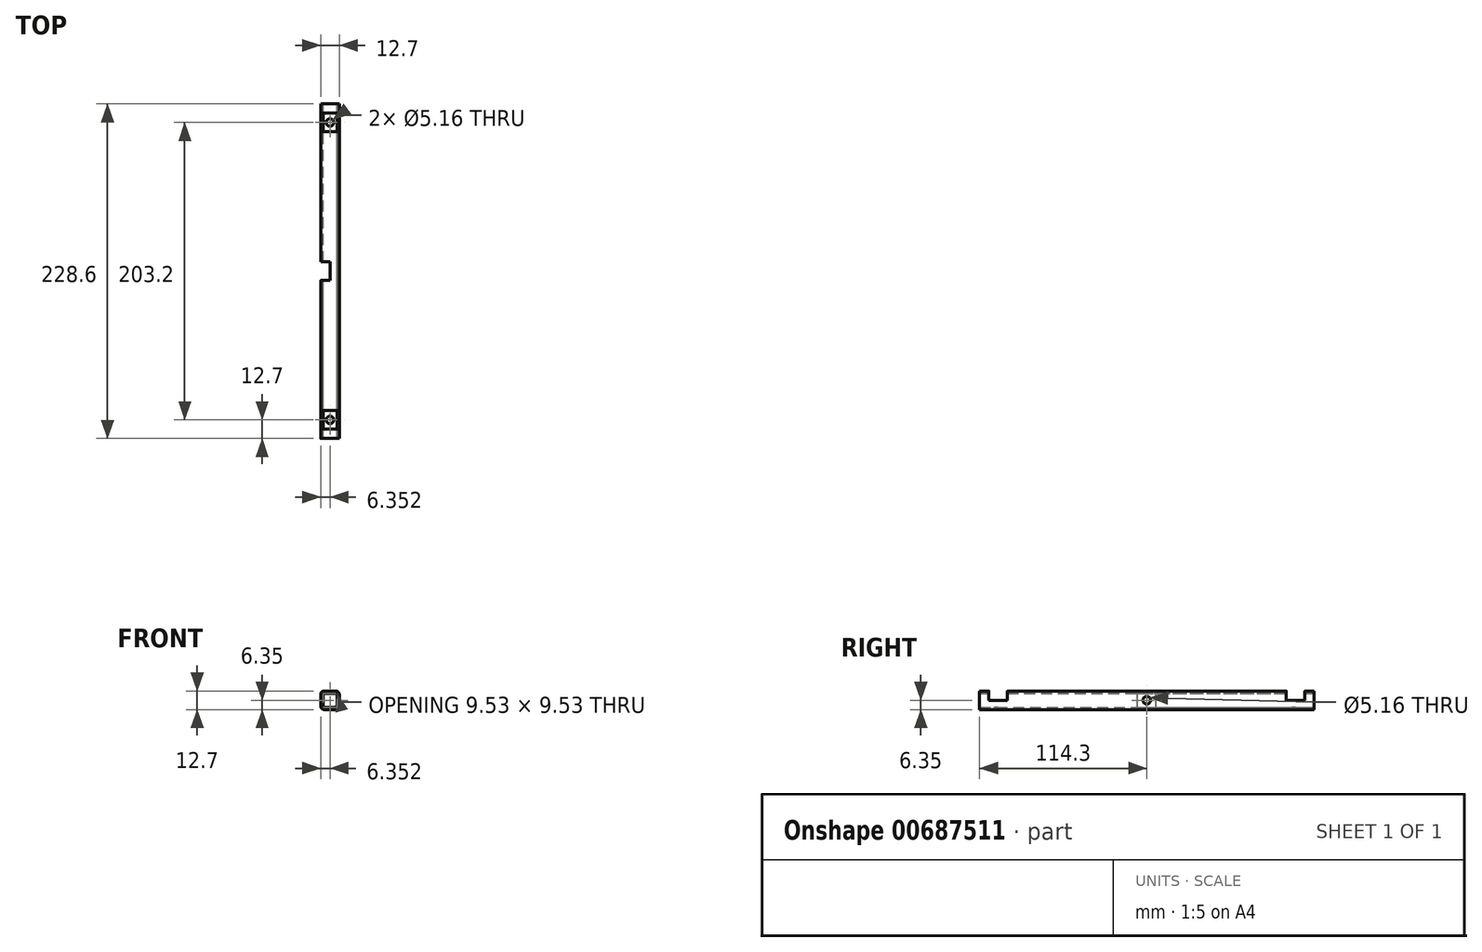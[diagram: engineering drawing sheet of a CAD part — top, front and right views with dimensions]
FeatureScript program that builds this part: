
annotation { "Feature Type Name" : "Feature", "Feature Type Description" : "" }
export const myFeature = defineFeature(function(context is Context, id is Id, definition is map)
    precondition{}
    {
        {
            var Q0;
            Q0=qCreatedBy(makeId("Front.planeOp"),FACE);
            var sketch = newSketch(context, id + "F0", { "sketchPlane" : qUnion([Q0])});
            skLineSegment(sketch, "E0.bottom", {"start": v(7.7, 0) * mm, "end": v(-0.25, 0) * mm});
            skLineSegment(sketch, "E0.top", {"start": v(7.7, -12.7) * mm, "end": v(-0.25, -12.7) * mm});
            skLineSegment(sketch, "E0.left", {"start": v(10.07, -2.38) * mm, "end": v(10.07, -10.32) * mm});
            skLineSegment(sketch, "E0.right", {"start": v(-2.63, -2.38) * mm, "end": v(-2.63, -10.32) * mm});
            skPoint(sketch, "E0.middle", {"position": v(3.72, -6.35) * mm});
            skPoint(sketch, "E1.visualSharp", {"position": v(-2.63, 0) * mm});
            skArc(sketch, "E1.filletArc", {"start": v(-0.25, 0) * mm, "mid": v(-1.93, -0.7) * mm, "end": v(-2.63, -2.38) * mm});
            skPoint(sketch, "E2.visualSharp", {"position": v(-2.63, -12.7) * mm});
            skArc(sketch, "E2.filletArc", {"start": v(-2.63, -10.32) * mm, "mid": v(-1.93, -12) * mm, "end": v(-0.25, -12.7) * mm});
            skPoint(sketch, "E3.visualSharp", {"position": v(10.07, -12.7) * mm});
            skArc(sketch, "E3.filletArc", {"start": v(7.7, -12.7) * mm, "mid": v(9.37, -12) * mm, "end": v(10.07, -10.32) * mm});
            skPoint(sketch, "E4.visualSharp", {"position": v(10.07, 0) * mm});
            skArc(sketch, "E4.filletArc", {"start": v(10.07, -2.38) * mm, "mid": v(9.37, -0.7) * mm, "end": v(7.7, 0) * mm});
            skLineSegment(sketch, "E5.bottom", {"start": v(6.9, -1.59) * mm, "end": v(0.55, -1.59) * mm});
            skLineSegment(sketch, "E5.top", {"start": v(6.9, -11.11) * mm, "end": v(0.55, -11.11) * mm});
            skLineSegment(sketch, "E5.left", {"start": v(8.48, -3.17) * mm, "end": v(8.48, -9.53) * mm});
            skLineSegment(sketch, "E5.right", {"start": v(-1.04, -3.18) * mm, "end": v(-1.04, -9.53) * mm});
            skPoint(sketch, "E6.visualSharp", {"position": v(-1.04, -1.59) * mm});
            skArc(sketch, "E6.filletArc", {"start": v(0.55, -1.59) * mm, "mid": v(-0.58, -2.05) * mm, "end": v(-1.04, -3.18) * mm});
            skPoint(sketch, "E7.visualSharp", {"position": v(8.48, -1.59) * mm});
            skArc(sketch, "E7.filletArc", {"start": v(8.48, -3.17) * mm, "mid": v(8.02, -2.05) * mm, "end": v(6.9, -1.59) * mm});
            skPoint(sketch, "E8.visualSharp", {"position": v(8.48, -11.11) * mm});
            skArc(sketch, "E8.filletArc", {"start": v(6.9, -11.11) * mm, "mid": v(8.02, -10.65) * mm, "end": v(8.48, -9.53) * mm});
            skPoint(sketch, "E9.visualSharp", {"position": v(-1.04, -11.11) * mm});
            skArc(sketch, "E9.filletArc", {"start": v(-1.04, -9.53) * mm, "mid": v(-0.58, -10.65) * mm, "end": v(0.55, -11.11) * mm});
            skSolve(sketch);
        }
        {
            var Q0;
            Q0=qSketchRegion(id+"F0",true);
            extrude(context, id + "F1", {"entities" : qUnion([Q0]), "depth" : 228.6 * mm, "offsetDistance" : 25.4 * mm});
        }
        {
            var Q0;
            Q0=qCreatedBy(makeId("Right.planeOp"),FACE);
            var sketch = newSketch(context, id + "F2", { "sketchPlane" : qUnion([Q0])});
            skLineSegment(sketch, "E10.bottom", {"start": v(-222.25, 0) * mm, "end": v(-209.55, 0) * mm});
            skLineSegment(sketch, "E10.top", {"start": v(-222.25, -6.35) * mm, "end": v(-209.55, -6.35) * mm});
            skLineSegment(sketch, "E10.left", {"start": v(-222.25, 0) * mm, "end": v(-222.25, -6.35) * mm});
            skLineSegment(sketch, "E10.right", {"start": v(-209.55, 0) * mm, "end": v(-209.55, -6.35) * mm});
            skLineSegment(sketch, "E11.bottom", {"start": v(-6.35, 0) * mm, "end": v(-19.05, 0) * mm});
            skLineSegment(sketch, "E11.top", {"start": v(-6.35, -6.35) * mm, "end": v(-19.05, -6.35) * mm});
            skLineSegment(sketch, "E11.left", {"start": v(-6.35, 0) * mm, "end": v(-6.35, -6.35) * mm});
            skLineSegment(sketch, "E11.right", {"start": v(-19.05, 0) * mm, "end": v(-19.05, -6.35) * mm});
            skSolve(sketch);
        }
        {
            var Q0;
            Q0=qSketchRegion(id+"F2",true);
            extrude(context, id + "F3", {"entities" : qUnion([Q0]), "operationType" : NewBodyOperationType.REMOVE, "depth" : 11.94 * mm, "offsetDistance" : 25.4 * mm, "hasSecondDirection" : true, "secondDirectionOppositeDirection" : true, "secondDirectionDepth" : 25.4 * mm});
        }
        {
            var Q0;
            Q0=qCreatedBy(makeId("Top.planeOp"),FACE);
            var sketch = newSketch(context, id + "F4", { "sketchPlane" : qUnion([Q0])});
            skLineSegment(sketch, "E12.bottom", {"start": v(3.72, -107.95) * mm, "end": v(-2.63, -107.95) * mm});
            skLineSegment(sketch, "E12.top", {"start": v(3.72, -120.65) * mm, "end": v(-2.63, -120.65) * mm});
            skLineSegment(sketch, "E12.left", {"start": v(3.72, -107.95) * mm, "end": v(3.72, -120.65) * mm});
            skLineSegment(sketch, "E12.right", {"start": v(-2.63, -107.95) * mm, "end": v(-2.63, -120.65) * mm});
            skSolve(sketch);
        }
        {
            var Q0;
            Q0=qSketchRegion(id+"F4",true);
            extrude(context, id + "F5", {"entities" : qUnion([Q0]), "operationType" : NewBodyOperationType.REMOVE, "oppositeDirection" : true, "depth" : 12.7 * mm, "offsetDistance" : 25.4 * mm});
        }
        {
            var Q0;
            Q0=qCreatedBy(makeId("Top.planeOp"),FACE);
            var sketch = newSketch(context, id + "F6", { "sketchPlane" : qUnion([Q0])});
            skCircle(sketch, "E13", {"center": v(3.72, -12.7) * mm, "radius": 2.58 * mm});
            skCircle(sketch, "E14", {"center": v(3.72, -215.9) * mm, "radius": 2.58 * mm});
            skSolve(sketch);
        }
        {
            var Q0;
            Q0=qSketchRegion(id+"F6",true);
            extrude(context, id + "F7", {"entities" : qUnion([Q0]), "operationType" : NewBodyOperationType.REMOVE, "oppositeDirection" : true, "depth" : 12.7 * mm, "offsetDistance" : 25.4 * mm});
        }
        {
            var Q0;
            Q0=qCreatedBy(makeId("Right.planeOp"),FACE);
            var sketch = newSketch(context, id + "F8", { "sketchPlane" : qUnion([Q0])});
            skCircle(sketch, "E15", {"center": v(-114.3, -6.35) * mm, "radius": 2.58 * mm});
            skSolve(sketch);
        }
        {
            var Q0;
            Q0=qSketchRegion(id+"F8",true);
            extrude(context, id + "F9", {"entities" : qUnion([Q0]), "operationType" : NewBodyOperationType.REMOVE, "depth" : 12.7 * mm, "offsetDistance" : 25.4 * mm});
        }
    });
